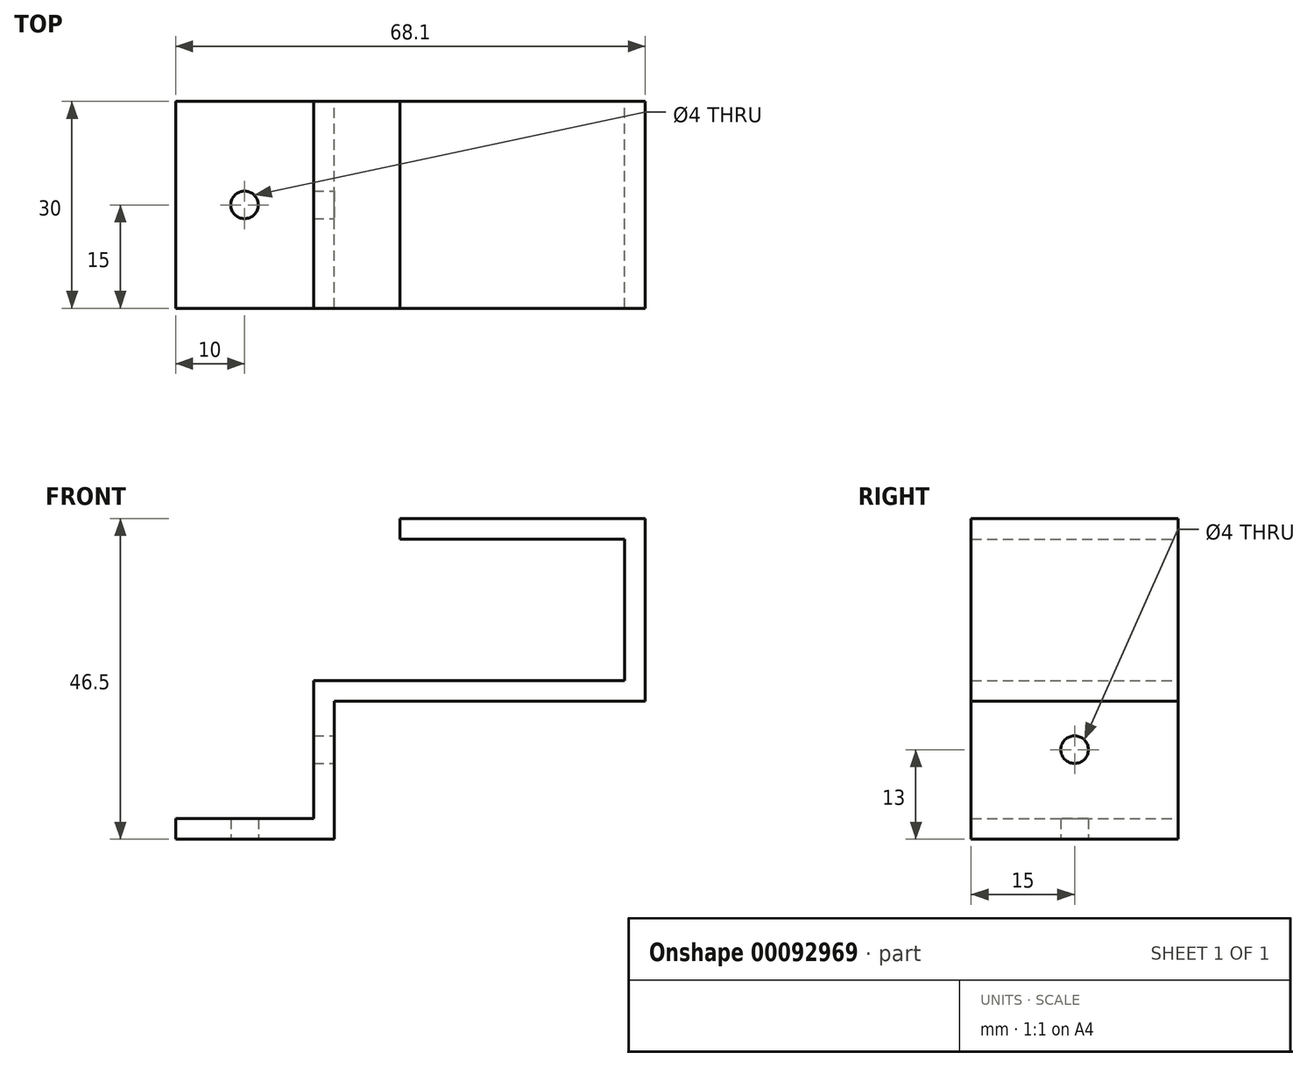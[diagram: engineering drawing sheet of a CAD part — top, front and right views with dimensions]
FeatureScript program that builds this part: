
annotation { "Feature Type Name" : "Feature", "Feature Type Description" : "" }
export const myFeature = defineFeature(function(context is Context, id is Id, definition is map)
    precondition{}
    {
        {
            var Q0;
            Q0=qCreatedBy(makeId("Front.planeOp"),FACE);
            var sketch = newSketch(context, id + "F0", { "sketchPlane" : qUnion([Q0])});
            skLineSegment(sketch, "E0.bottom", {"start": v(-10, 10) * mm, "end": v(10, 10) * mm, "construction": true});
            skLineSegment(sketch, "E0.top", {"start": v(-10, -10) * mm, "end": v(10, -10) * mm, "construction": true});
            skLineSegment(sketch, "E0.left", {"start": v(-10, 10) * mm, "end": v(-10, -10) * mm, "construction": true});
            skLineSegment(sketch, "E0.right", {"start": v(10, 10) * mm, "end": v(10, -10) * mm, "construction": true});
            skPoint(sketch, "E0.middle", {"position": v(0, 0) * mm});
            skLineSegment(sketch, "E1.bottom", {"start": v(-10, 10) * mm, "end": v(55.1, 10) * mm, "construction": true});
            skLineSegment(sketch, "E1.top", {"start": v(-10, 30.5) * mm, "end": v(55.1, 30.5) * mm, "construction": true});
            skLineSegment(sketch, "E1.left", {"start": v(-10, 10) * mm, "end": v(-10, 30.5) * mm, "construction": true});
            skLineSegment(sketch, "E1.right", {"start": v(55.1, 10) * mm, "end": v(55.1, 30.5) * mm, "construction": true});
            skLineSegment(sketch, "E2", {"start": v(-10, -10) * mm, "end": v(10, -10) * mm});
            skLineSegment(sketch, "E3", {"start": v(10, -10) * mm, "end": v(10, 10) * mm});
            skLineSegment(sketch, "E4", {"start": v(10, 10) * mm, "end": v(55.1, 10) * mm});
            skLineSegment(sketch, "E5", {"start": v(55.1, 10) * mm, "end": v(55.1, 30.5) * mm});
            skLineSegment(sketch, "E6", {"start": v(55.1, 30.5) * mm, "end": v(22.55, 30.5) * mm});
            skLineSegment(sketch, "E7.0", {"start": v(58.1, 33.5) * mm, "end": v(22.55, 33.5) * mm});
            skLineSegment(sketch, "E7.1", {"start": v(-10, -13) * mm, "end": v(13, -13) * mm});
            skLineSegment(sketch, "E7.2", {"start": v(13, -13) * mm, "end": v(13, 7) * mm});
            skLineSegment(sketch, "E7.3", {"start": v(13, 7) * mm, "end": v(58.1, 7) * mm});
            skLineSegment(sketch, "E7.4", {"start": v(58.1, 7) * mm, "end": v(58.1, 33.5) * mm});
            skLineSegment(sketch, "E8", {"start": v(22.55, 33.5) * mm, "end": v(22.55, 30.5) * mm});
            skLineSegment(sketch, "E9", {"start": v(-10, -13) * mm, "end": v(-10, -10) * mm});
            skSolve(sketch);
        }
        {
            var Q0;
            Q0 = qSketchRegion(id + "F0", true);
            extrude(context, id + "F1", {"entities" : qUnion([Q0]), "depth" : 15 * mm, "hasSecondDirection" : true, "secondDirectionOppositeDirection" : true, "secondDirectionDepth" : 15 * mm});
        }
        {
            var Q0;
            Q0=makeQuery(id+"F1.opExtrude","SWEPT_FACE",FACE,{"disambiguationData":[OSD([sQuery(id+"F0.wireOp",EDGE,"E7.2")])]});
            var sketch = newSketch(context, id + "F2", { "sketchPlane" : qUnion([Q0])});
            skCircle(sketch, "E10", {"center": v(0, 0) * mm, "radius": 2 * mm});
            skSolve(sketch);
        }
        {
            var Q0;
            Q0 = qSketchRegion(id + "F2", true);
            extrude(context, id + "F3", {"entities" : qUnion([Q0]), "operationType" : NewBodyOperationType.REMOVE, "oppositeDirection" : true, "depth" : 5 * mm, "hasSecondDirection" : true, "secondDirectionOppositeDirection" : false, "secondDirectionDepth" : 5 * mm});
        }
        {
            var Q0;
            Q0=makeQuery(id+"F1.opExtrude","SWEPT_FACE",FACE,{"disambiguationData":[OSD([sQuery(id+"F0.wireOp",EDGE,"E7.1")])]});
            var sketch = newSketch(context, id + "F4", { "sketchPlane" : qUnion([Q0])});
            skCircle(sketch, "E11", {"center": v(0, 0) * mm, "radius": 2 * mm});
            skSolve(sketch);
        }
        {
            var Q0;
            Q0 = qSketchRegion(id + "F4", true);
            extrude(context, id + "F5", {"entities" : qUnion([Q0]), "operationType" : NewBodyOperationType.REMOVE, "oppositeDirection" : true, "depth" : 5 * mm, "hasSecondDirection" : true, "secondDirectionOppositeDirection" : false, "secondDirectionDepth" : 5 * mm});
        }
    });
